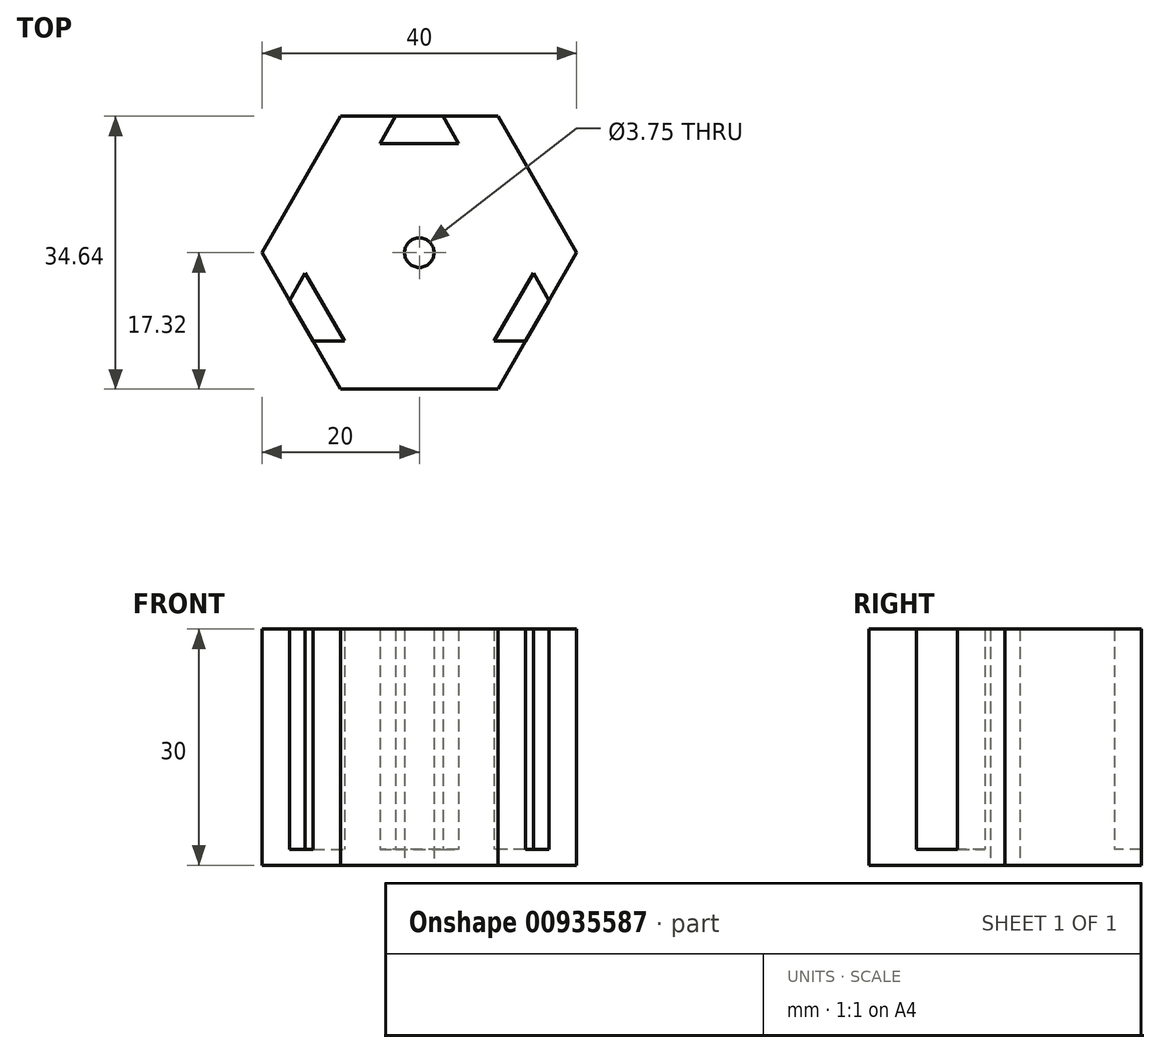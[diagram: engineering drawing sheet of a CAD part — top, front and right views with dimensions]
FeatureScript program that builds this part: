
annotation { "Feature Type Name" : "Feature", "Feature Type Description" : "" }
export const myFeature = defineFeature(function(context is Context, id is Id, definition is map)
    precondition{}
    {
        {
            var Q0;
            Q0=qCreatedBy(makeId("Top.planeOp"),FACE);
            var sketch = newSketch(context, id + "F0", { "sketchPlane" : qUnion([Q0])});
            skCircle(sketch, "E0.cCircle", {"center": v(0, 0) * mm, "radius": 17.32 * mm, "construction": true});
            skLineSegment(sketch, "E0.0", {"start": v(-10, 17.32) * mm, "end": v(10, 17.32) * mm});
            skLineSegment(sketch, "E0.1", {"start": v(10, 17.32) * mm, "end": v(20, 0) * mm});
            skLineSegment(sketch, "E0.2", {"start": v(20, 0) * mm, "end": v(10, -17.32) * mm});
            skLineSegment(sketch, "E0.3", {"start": v(10, -17.32) * mm, "end": v(-10, -17.32) * mm});
            skLineSegment(sketch, "E0.4", {"start": v(-10, -17.32) * mm, "end": v(-20, 0) * mm});
            skLineSegment(sketch, "E0.5", {"start": v(-20, 0) * mm, "end": v(-10, 17.32) * mm});
            skPoint(sketch, "E0.0.midPoint", {"position": v(0, 17.32) * mm});
            skLineSegment(sketch, "E1", {"start": v(-3, 17.32) * mm, "end": v(3, 17.32) * mm});
            skLineSegment(sketch, "E2", {"start": v(3, 17.32) * mm, "end": v(5, 13.86) * mm});
            skLineSegment(sketch, "E3", {"start": v(5, 13.86) * mm, "end": v(-5, 13.86) * mm});
            skLineSegment(sketch, "E4", {"start": v(-5, 13.86) * mm, "end": v(-3, 17.32) * mm});
            skLineSegment(sketch, "E5.1.0", {"start": v(-16.5, -6.06) * mm, "end": v(-14.5, -2.6) * mm});
            skLineSegment(sketch, "E5.1.1", {"start": v(-14.5, -2.6) * mm, "end": v(-9.5, -11.26) * mm});
            skLineSegment(sketch, "E5.1.2", {"start": v(-9.5, -11.26) * mm, "end": v(-13.5, -11.26) * mm});
            skLineSegment(sketch, "E5.2.0", {"start": v(13.5, -11.26) * mm, "end": v(9.5, -11.26) * mm});
            skLineSegment(sketch, "E5.2.1", {"start": v(9.5, -11.26) * mm, "end": v(14.5, -2.6) * mm});
            skLineSegment(sketch, "E5.2.2", {"start": v(14.5, -2.6) * mm, "end": v(16.5, -6.06) * mm});
            skCircle(sketch, "E6", {"center": v(0, 0) * mm, "radius": 1.88 * mm});
            skSolve(sketch);
        }
        {
            var Q0;
            {var subQ11=sQuery(id+"F0.wireOp",EDGE,"E0.1");Q0=makeQuery(id+"F0.imprint","IMPRINT",FACE,{"disambiguationData":[TD([[makeQuery(id+"F0.imprint","IMPRINT",EDGE,{"derivedFrom":subQ11}),-1.0]])]});}
            extrude(context, id + "F1", {"entities" : qUnion([Q0]), "depth" : 30 * mm, "offsetDistance" : 25 * mm, "hasSecondDirection" : true, "secondDirectionOppositeDirection" : true, "secondDirectionDepth" : 0 * mm});
        }
        {
            var Q0;
            Q0 = qSketchRegion(id + "F0", true);
            extrude(context, id + "F2", {"entities" : qUnion([Q0]), "operationType" : NewBodyOperationType.ADD, "depth" : 2 * mm, "offsetDistance" : 25 * mm});
        }
    });
